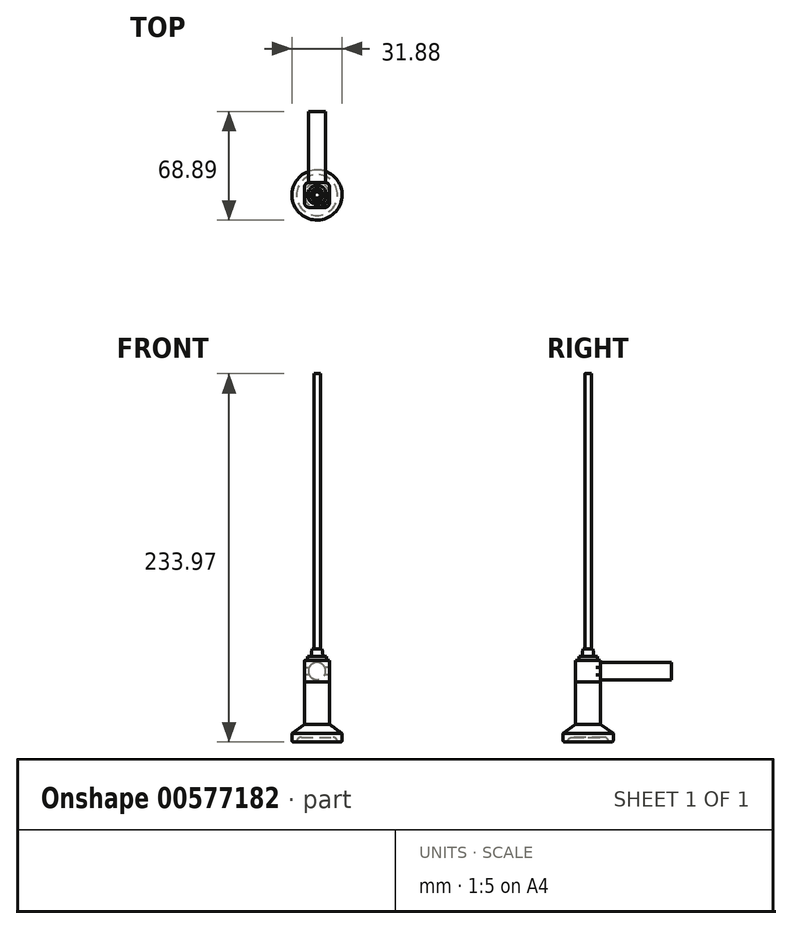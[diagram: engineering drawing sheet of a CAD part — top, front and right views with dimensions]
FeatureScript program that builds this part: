
annotation { "Feature Type Name" : "Feature", "Feature Type Description" : "" }
export const myFeature = defineFeature(function(context is Context, id is Id, definition is map)
    precondition{}
    {
        {
            var Q0;
            Q0=qCreatedBy(makeId("Top.planeOp"),FACE);
            var sketch = newSketch(context, id + "F0", { "sketchPlane" : qUnion([Q0])});
            skCircle(sketch, "E0", {"center": v(0, 0) * mm, "radius": 15.94 * mm});
            skSolve(sketch);
        }
        {
            var Q0;
            Q0 = qSketchRegion(id + "F0", true);
            extrude(context, id + "F1", {"entities" : qUnion([Q0]), "depth" : 5.34 * mm, "offsetDistance" : 25 * mm});
        }
        {
            var Q0;
            Q0=makeQuery(id+"F1.opExtrude","CAP_FACE",FACE,{"disambiguationData":[OSD([sQuery(id+"F0.wireOp",EDGE,"E0")])],"isStart":false});
            cPlane(context, id + "F2", {"entities" : qUnion([Q0]), "cplaneType" : CPlaneType.OFFSET, "offset" : 5.84 * mm, "width" : 150 * mm, "height" : 150 * mm});
        }
        {
            var Q0;
            Q0=qCreatedBy(id+"F2.planeOp",FACE);
            var sketch = newSketch(context, id + "F3", { "sketchPlane" : qUnion([Q0])});
            skCircle(sketch, "E1", {"center": v(0, 0) * mm, "radius": 7.95 * mm});
            skSolve(sketch);
        }
        {
            var Q1;
            Q1=makeQuery(id+"F1.opExtrude","CAP_FACE",FACE,{"disambiguationData":[OSD([sQuery(id+"F0.wireOp",EDGE,"E0")])],"isStart":false});
            var Q2;
            Q2=makeQuery(id+"F3.imprint","IMPRINT",FACE,{"disambiguationData":[TD([[makeQuery(id+"F3.imprint","IMPRINT",EDGE,{"derivedFrom":sQuery(id+"F3.wireOp",EDGE,"E1")}),1.0]])]});
            loft(context, id + "F4", {"operationType" : NewBodyOperationType.ADD, "sheetProfilesArray" : [{ "sheetProfileEntities" : qUnion([Q1]) }, { "sheetProfileEntities" : qUnion([Q2]) }]});
        }
        {
            var Q0;
            Q0=makeQuery(id+"F4.opLoft","CAP_FACE",FACE,{"disambiguationData":[OSD([makeQuery(id+"F3.imprint","IMPRINT",FACE,{"disambiguationData":[TD([[makeQuery(id+"F3.imprint","IMPRINT",EDGE,{"derivedFrom":sQuery(id+"F3.wireOp",EDGE,"E1")}),1.0]])]})])],"isStart":true});
            extrude(context, id + "F5", {"entities" : qUnion([Q0]), "operationType" : NewBodyOperationType.ADD, "depth" : 27 * mm, "offsetDistance" : 25 * mm});
        }
        {
            var Q0;
            Q0=makeQuery(id+"F5.opExtrude","CAP_FACE",FACE,{"disambiguationData":[OSD([makeQuery(id+"F3.imprint","IMPRINT",FACE,{"disambiguationData":[TD([[makeQuery(id+"F3.imprint","IMPRINT",EDGE,{"derivedFrom":sQuery(id+"F3.wireOp",EDGE,"E1")}),1.0]])]})])],"isStart":false});
            cPlane(context, id + "F6", {"entities" : qUnion([Q0]), "cplaneType" : CPlaneType.OFFSET, "offset" : 0 * mm, "width" : 150 * mm, "height" : 150 * mm});
        }
        {
            var Q0;
            Q0=qCreatedBy(id+"F6.planeOp",FACE);
            var sketch = newSketch(context, id + "F7", { "sketchPlane" : qUnion([Q0])});
            skLineSegment(sketch, "E2.bottom", {"start": v(7.95, -7.95) * mm, "end": v(-7.95, -7.95) * mm});
            skLineSegment(sketch, "E2.top", {"start": v(7.95, 7.95) * mm, "end": v(-7.95, 7.95) * mm});
            skLineSegment(sketch, "E2.left", {"start": v(7.95, -7.95) * mm, "end": v(7.95, 7.95) * mm});
            skLineSegment(sketch, "E2.right", {"start": v(-7.95, -7.95) * mm, "end": v(-7.95, 7.95) * mm});
            skPoint(sketch, "E2.middle", {"position": v(0, 0) * mm});
            skSolve(sketch);
        }
        {
            var Q0;
            Q0=makeQuery(id+"F7.imprint","IMPRINT",FACE,{"disambiguationData":[TD([[makeQuery(id+"F7.imprint","IMPRINT",EDGE,{"derivedFrom":sQuery(id+"F7.wireOp",EDGE,"E2.bottom")}),-1.0]])]});
            extrude(context, id + "F8", {"entities" : qUnion([Q0]), "operationType" : NewBodyOperationType.ADD, "depth" : 13.7 * mm, "offsetDistance" : 25 * mm});
        }
        {
            var Q0;
            Q0=makeQuery(id+"F8.opExtrude","SWEPT_FACE",FACE,{"disambiguationData":[OSD([sQuery(id+"F7.wireOp",EDGE,"E2.top")])]});
            cPlane(context, id + "F9", {"entities" : qUnion([Q0]), "cplaneType" : CPlaneType.OFFSET, "offset" : 0 * mm, "width" : 150 * mm, "height" : 150 * mm});
        }
        {
            var Q0;
            Q0=qCreatedBy(id+"F9.planeOp",FACE);
            var sketch = newSketch(context, id + "F10", { "sketchPlane" : qUnion([Q0])});
            skPoint(sketch, "E3", {"position": v(0, 45.03) * mm});
            skCircle(sketch, "E4", {"center": v(0, 45.03) * mm, "radius": 5.5 * mm});
            skSolve(sketch);
        }
        {
            var Q0;
            Q0=makeQuery(id+"F10.imprint","IMPRINT",FACE,{"disambiguationData":[TD([[makeQuery(id+"F10.imprint","IMPRINT",EDGE,{"derivedFrom":sQuery(id+"F10.wireOp",EDGE,"E4")}),1.0]])]});
            extrude(context, id + "F11", {"entities" : qUnion([Q0]), "operationType" : NewBodyOperationType.ADD, "depth" : 45 * mm, "offsetDistance" : 25 * mm});
        }
        {
            var Q0;
            Q0=makeQuery(id+"F8.opExtrude","CAP_FACE",FACE,{"disambiguationData":[OSD([sQuery(id+"F7.wireOp",EDGE,"E2.bottom"),sQuery(id+"F7.wireOp",EDGE,"E2.top"),sQuery(id+"F7.wireOp",EDGE,"E2.left"),sQuery(id+"F7.wireOp",EDGE,"E2.right")])],"isStart":false});
            cPlane(context, id + "F12", {"entities" : qUnion([Q0]), "cplaneType" : CPlaneType.OFFSET, "offset" : 0 * mm, "width" : 150 * mm, "height" : 150 * mm});
        }
        {
            var Q0;
            Q0=qCreatedBy(id+"F12.planeOp",FACE);
            var sketch = newSketch(context, id + "F13", { "sketchPlane" : qUnion([Q0])});
            skCircle(sketch, "E5", {"center": v(0, 0) * mm, "radius": 5.97 * mm});
            skSolve(sketch);
        }
        {
            var Q0;
            Q0=makeQuery(id+"F13.imprint","IMPRINT",FACE,{"disambiguationData":[TD([[makeQuery(id+"F13.imprint","IMPRINT",EDGE,{"derivedFrom":sQuery(id+"F13.wireOp",EDGE,"E5")}),1.0]])]});
            extrude(context, id + "F14", {"entities" : qUnion([Q0]), "operationType" : NewBodyOperationType.ADD, "depth" : 2.5 * mm, "offsetDistance" : 25 * mm});
        }
        {
            var Q0;
            Q0=makeQuery(id+"F14.opExtrude","CAP_FACE",FACE,{"disambiguationData":[OSD([sQuery(id+"F13.wireOp",EDGE,"E5")])],"isStart":false});
            cPlane(context, id + "F15", {"entities" : qUnion([Q0]), "cplaneType" : CPlaneType.OFFSET, "offset" : 0 * mm, "width" : 150 * mm, "height" : 150 * mm});
        }
        {
            var Q0;
            Q0=qCreatedBy(id+"F15.planeOp",FACE);
            var sketch = newSketch(context, id + "F16", { "sketchPlane" : qUnion([Q0])});
            skCircle(sketch, "E6", {"center": v(0, 0) * mm, "radius": 3.8 * mm});
            skSolve(sketch);
        }
        {
            var Q0;
            Q0=makeQuery(id+"F16.imprint","IMPRINT",FACE,{"disambiguationData":[TD([[makeQuery(id+"F16.imprint","IMPRINT",EDGE,{"derivedFrom":sQuery(id+"F16.wireOp",EDGE,"E6")}),1.0]])]});
            cPlane(context, id + "F17", {"entities" : qUnion([Q0]), "cplaneType" : CPlaneType.OFFSET, "offset" : 4.6 * mm, "width" : 150 * mm, "height" : 150 * mm});
        }
        {
            var Q0;
            Q0=qCreatedBy(id+"F17.planeOp",FACE);
            var sketch = newSketch(context, id + "F18", { "sketchPlane" : qUnion([Q0])});
            skCircle(sketch, "E7", {"center": v(0, 0) * mm, "radius": 3.2 * mm});
            skSolve(sketch);
        }
        {
            var Q1;
            Q1=makeQuery(id+"F16.imprint","IMPRINT",FACE,{"disambiguationData":[TD([[makeQuery(id+"F16.imprint","IMPRINT",EDGE,{"derivedFrom":sQuery(id+"F16.wireOp",EDGE,"E6")}),1.0]])]});
            var Q2;
            Q2=makeQuery(id+"F18.imprint","IMPRINT",FACE,{"disambiguationData":[TD([[makeQuery(id+"F18.imprint","IMPRINT",EDGE,{"derivedFrom":sQuery(id+"F18.wireOp",EDGE,"E7")}),1.0]])]});
            loft(context, id + "F19", {"operationType" : NewBodyOperationType.ADD, "sheetProfilesArray" : [{ "sheetProfileEntities" : qUnion([Q1]) }, { "sheetProfileEntities" : qUnion([Q2]) }]});
        }
        {
            var Q0;
            Q0=makeQuery(id+"F19.opLoft","CAP_FACE",FACE,{"disambiguationData":[OSD([makeQuery(id+"F18.imprint","IMPRINT",FACE,{"disambiguationData":[TD([[makeQuery(id+"F18.imprint","IMPRINT",EDGE,{"derivedFrom":sQuery(id+"F18.wireOp",EDGE,"E7")}),1.0]])]})])],"isStart":true});
            cPlane(context, id + "F20", {"entities" : qUnion([Q0]), "cplaneType" : CPlaneType.OFFSET, "offset" : 0 * mm, "width" : 150 * mm, "height" : 150 * mm});
        }
        {
            var Q0;
            Q0=qCreatedBy(id+"F20.planeOp",FACE);
            var sketch = newSketch(context, id + "F21", { "sketchPlane" : qUnion([Q0])});
            skCircle(sketch, "E8", {"center": v(0, 0) * mm, "radius": 2.05 * mm});
            skSolve(sketch);
        }
        {
            var Q0;
            Q0=makeQuery(id+"F21.imprint","IMPRINT",FACE,{"disambiguationData":[TD([[makeQuery(id+"F21.imprint","IMPRINT",EDGE,{"derivedFrom":sQuery(id+"F21.wireOp",EDGE,"E8")}),1.0]])]});
            extrude(context, id + "F22", {"entities" : qUnion([Q0]), "operationType" : NewBodyOperationType.ADD, "depth" : 175 * mm, "offsetDistance" : 25 * mm});
        }
        {
            var Q0;
            Q0=makeQuery(id+"F8.opExtrude","SWEPT_EDGE",EDGE,{"disambiguationData":[OSD([sQuery(id+"F7.wireOp",EDGE,"E2.bottom"),sQuery(id+"F7.wireOp",EDGE,"E2.right")])]});
            var Q1;
            Q1=makeQuery(id+"F8.opExtrude","SWEPT_EDGE",EDGE,{"disambiguationData":[OSD([sQuery(id+"F7.wireOp",EDGE,"E2.top"),sQuery(id+"F7.wireOp",EDGE,"E2.right")])]});
            var Q2;
            Q2=makeQuery(id+"F8.opExtrude","SWEPT_EDGE",EDGE,{"disambiguationData":[OSD([sQuery(id+"F7.wireOp",EDGE,"E2.bottom"),sQuery(id+"F7.wireOp",EDGE,"E2.left")])]});
            var Q3;
            Q3=makeQuery(id+"F8.opExtrude","SWEPT_EDGE",EDGE,{"disambiguationData":[OSD([sQuery(id+"F7.wireOp",EDGE,"E2.top"),sQuery(id+"F7.wireOp",EDGE,"E2.left")])]});
            fillet(context, id + "F23", {"entities" : qUnion([Q0, Q1, Q2, Q3]), "radius" : 3 * mm, "tangentPropagation" : true, "allowEdgeOverflow" : false});
        }
        {
            var Q0;
            Q0=makeQuery(id+"F1.opExtrude","CAP_EDGE",EDGE,{"disambiguationData":[OSD([sQuery(id+"F0.wireOp",EDGE,"E0")])],"isStart":true});
            fillet(context, id + "F24", {"entities" : qUnion([Q0]), "radius" : 1 * mm, "tangentPropagation" : true, "allowEdgeOverflow" : false});
        }
        {
            var Q0;
            Q0=makeQuery(id+"F1.opExtrude","CAP_FACE",FACE,{"disambiguationData":[OSD([sQuery(id+"F0.wireOp",EDGE,"E0")])],"isStart":true});
            cPlane(context, id + "F25", {"entities" : qUnion([Q0]), "cplaneType" : CPlaneType.OFFSET, "offset" : 0 * mm, "width" : 150 * mm, "height" : 150 * mm});
        }
        {
            var Q0;
            Q0=qCreatedBy(id+"F25.planeOp",FACE);
            var sketch = newSketch(context, id + "F26", { "sketchPlane" : qUnion([Q0])});
            skCircle(sketch, "E9", {"center": v(0, 0) * mm, "radius": 13 * mm});
            skSolve(sketch);
        }
        {
            var Q0;
            Q0=makeQuery(id+"F26.imprint","IMPRINT",FACE,{"disambiguationData":[TD([[makeQuery(id+"F26.imprint","IMPRINT",EDGE,{"derivedFrom":sQuery(id+"F26.wireOp",EDGE,"E9")}),1.0]])]});
            extrude(context, id + "F27", {"entities" : qUnion([Q0]), "operationType" : NewBodyOperationType.REMOVE, "oppositeDirection" : true, "depth" : 3 * mm, "offsetDistance" : 25 * mm});
        }
        {
            var Q0;
            Q0=makeQuery(id+"F27.boolean.opBoolean","COPY",EDGE,{"derivedFrom":makeQuery(id+"F27.opExtrude","CAP_EDGE",EDGE,{"disambiguationData":[OSD([sQuery(id+"F26.wireOp",EDGE,"E9")])],"isStart":false})});
            fillet(context, id + "F28", {"entities" : qUnion([Q0]), "radius" : 3 * mm, "tangentPropagation" : true, "allowEdgeOverflow" : false});
        }
        {
            var Q0;
            Q0=makeQuery(id+"F1.opExtrude","SWEPT_BODY",BODY,{"disambiguationData":[OSD([sQuery(id+"F0.wireOp",EDGE,"E0")])]});
            transform(context, id + "F29", {"entities" : qUnion([Q0]), "transformType" : TransformType.TRANSLATION_3D, "dx" : 0 * mm, "dy" : 0 * mm, "dz" : 0 * mm, "makeCopy" : true});
        }
        {
            var Q0;
            Q0=makeQuery(id+"F29.opPattern","COPY",BODY,{"derivedFrom":makeQuery(id+"F1.opExtrude","SWEPT_BODY",BODY,{"disambiguationData":[OSD([sQuery(id+"F0.wireOp",EDGE,"E0")])]}),"instanceName":"1"});
            deleteBodies(context, id + "F30", {"entities" : qUnion([Q0])});
        }
    });
